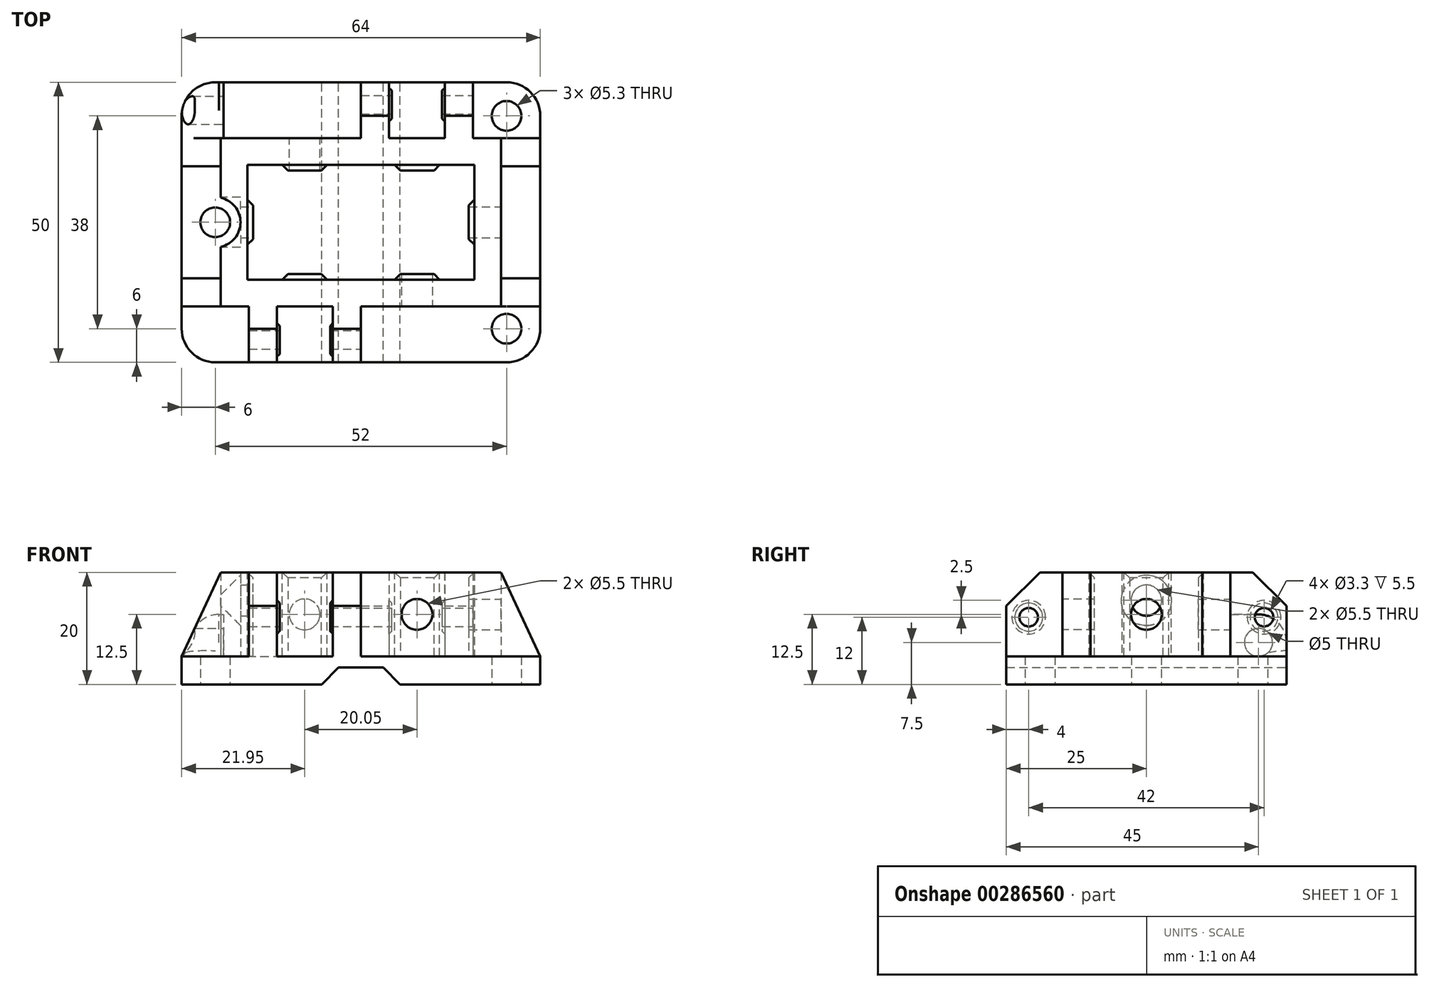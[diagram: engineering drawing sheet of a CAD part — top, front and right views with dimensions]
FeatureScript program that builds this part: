
annotation { "Feature Type Name" : "Feature", "Feature Type Description" : "" }
export const myFeature = defineFeature(function(context is Context, id is Id, definition is map)
    precondition{}
    {
        {
            var Q0;
            Q0=qCreatedBy(makeId("Top.planeOp"),FACE);
            var sketch = newSketch(context, id + "F0", { "sketchPlane" : qUnion([Q0])});
            skLineSegment(sketch, "E0.bottom", {"start": v(0, 0) * mm, "end": v(64, 0) * mm});
            skLineSegment(sketch, "E0.top", {"start": v(0, 50) * mm, "end": v(64, 50) * mm});
            skLineSegment(sketch, "E0.left", {"start": v(0, 0) * mm, "end": v(0, 50) * mm});
            skLineSegment(sketch, "E0.right", {"start": v(64, 0) * mm, "end": v(64, 50) * mm});
            skCircle(sketch, "E1", {"center": v(58, 44) * mm, "radius": 2.65 * mm});
            skPoint(sketch, "E2.centerSnap0", {"position": v(32, 0) * mm});
            skCircle(sketch, "E3", {"center": v(58, 6) * mm, "radius": 2.65 * mm});
            skCircle(sketch, "E4", {"center": v(6, 25) * mm, "radius": 2.65 * mm});
            skPoint(sketch, "E4.centerSnap0", {"position": v(0, 25) * mm});
            skSolve(sketch);
        }
        {
            var Q0;
            Q0=qSketchRegion(id+"F0",true);
            extrude(context, id + "F1", {"entities" : qUnion([Q0]), "depth" : 5 * mm});
        }
        {
            var Q0;
            Q0=makeQuery(id+"F1.opExtrude","CAP_FACE",FACE,{"disambiguationData":[OSD([sQuery(id+"F0.wireOp",EDGE,"E0.bottom"),sQuery(id+"F0.wireOp",EDGE,"E0.top"),sQuery(id+"F0.wireOp",EDGE,"E0.left"),sQuery(id+"F0.wireOp",EDGE,"E0.right"),sQuery(id+"F0.wireOp",EDGE,"SUFVuphh-Qgx9-THfo-SX6n-8QSMb4j17lpz"),sQuery(id+"F0.wireOp",EDGE,"E1"),sQuery(id+"F0.wireOp",EDGE,"E2")])],"isStart":false});
            var sketch = newSketch(context, id + "F2", { "sketchPlane" : qUnion([Q0])});
            skLineSegment(sketch, "E5.bottom", {"start": v(7, 40) * mm, "end": v(57, 40) * mm});
            skLineSegment(sketch, "E5.top", {"start": v(7, 10) * mm, "end": v(57, 10) * mm});
            skLineSegment(sketch, "E5.left", {"start": v(7, 40) * mm, "end": v(7, 29.39) * mm});
            skLineSegment(sketch, "E5.right", {"start": v(57, 40) * mm, "end": v(57, 10) * mm});
            skLineSegment(sketch, "E6.0.0", {"start": v(64, 50) * mm, "end": v(0, 50) * mm, "construction": true});
            skLineSegment(sketch, "E6.0.1", {"start": v(0, 50) * mm, "end": v(0, 0) * mm, "construction": true});
            skLineSegment(sketch, "E6.0.2", {"start": v(0, 0) * mm, "end": v(64, 0) * mm, "construction": true});
            skLineSegment(sketch, "E6.0.3", {"start": v(64, 0) * mm, "end": v(64, 50) * mm, "construction": true});
            skArc(sketch, "E7", {"start": v(7, 20.61) * mm, "mid": v(10.5, 25) * mm, "end": v(7, 29.39) * mm});
            skLineSegment(sketch, "E8.trimOffspring", {"start": v(7, 20.61) * mm, "end": v(7, 10) * mm});
            skLineSegment(sketch, "E9.bottom", {"start": v(11.75, 35.25) * mm, "end": v(52.25, 35.25) * mm});
            skLineSegment(sketch, "E9.top", {"start": v(11.75, 14.75) * mm, "end": v(52.25, 14.75) * mm});
            skLineSegment(sketch, "E9.left", {"start": v(11.75, 35.25) * mm, "end": v(11.75, 14.75) * mm});
            skLineSegment(sketch, "E9.right", {"start": v(52.25, 35.25) * mm, "end": v(52.25, 14.75) * mm});
            skSolve(sketch);
        }
        {
            var Q0;
            Q0=qSketchRegion(id+"F2",true);
            extrude(context, id + "F3", {"entities" : qUnion([Q0]), "operationType" : NewBodyOperationType.ADD, "depth" : 15 * mm});
        }
        {
            var Q0;
            Q0=makeQuery(id+"F3.opExtrude","CAP_FACE",FACE,{"disambiguationData":[OSD([sQuery(id+"F2.wireOp",EDGE,"E5.bottom"),sQuery(id+"F2.wireOp",EDGE,"E5.top"),sQuery(id+"F2.wireOp",EDGE,"E5.left"),sQuery(id+"F2.wireOp",EDGE,"E5.right"),sQuery(id+"F2.wireOp",EDGE,"E7"),sQuery(id+"F2.wireOp",EDGE,"E8.trimOffspring"),sQuery(id+"F2.wireOp",EDGE,"E9.bottom"),sQuery(id+"F2.wireOp",EDGE,"E9.top"),sQuery(id+"F2.wireOp",EDGE,"E9.left"),sQuery(id+"F2.wireOp",EDGE,"E9.right")])],"isStart":false});
            var sketch = newSketch(context, id + "F4", { "sketchPlane" : qUnion([Q0])});
            skLineSegment(sketch, "E10.bottom", {"start": v(11.75, 29) * mm, "end": v(12.75, 29) * mm});
            skLineSegment(sketch, "E10.top", {"start": v(11.75, 21) * mm, "end": v(12.75, 21) * mm});
            skLineSegment(sketch, "E10.left", {"start": v(11.75, 29) * mm, "end": v(11.75, 21) * mm});
            skLineSegment(sketch, "E10.right", {"start": v(12.75, 29) * mm, "end": v(12.75, 21) * mm});
            skLineSegment(sketch, "E11", {"start": v(32, 35.25) * mm, "end": v(32, 14.75) * mm, "construction": true});
            skLineSegment(sketch, "E12.MirrorCS", {"start": v(52.25, 29) * mm, "end": v(51.25, 29) * mm});
            skLineSegment(sketch, "E13.MirrorCS", {"start": v(52.25, 21) * mm, "end": v(51.25, 21) * mm});
            skLineSegment(sketch, "E14.MirrorCS", {"start": v(51.25, 29) * mm, "end": v(51.25, 21) * mm});
            skLineSegment(sketch, "E15.MirrorCS", {"start": v(52.25, 29) * mm, "end": v(52.25, 21) * mm});
            skLineSegment(sketch, "E16.bottom", {"start": v(38.05, 35.25) * mm, "end": v(46.05, 35.25) * mm});
            skLineSegment(sketch, "E16.top", {"start": v(38.05, 34.25) * mm, "end": v(46.05, 34.25) * mm});
            skLineSegment(sketch, "E16.left", {"start": v(38.05, 35.25) * mm, "end": v(38.05, 34.25) * mm});
            skLineSegment(sketch, "E16.right", {"start": v(46.05, 35.25) * mm, "end": v(46.05, 34.25) * mm});
            skLineSegment(sketch, "E17.bottom", {"start": v(17.95, 35.25) * mm, "end": v(25.95, 35.25) * mm});
            skLineSegment(sketch, "E17.top", {"start": v(17.95, 34.25) * mm, "end": v(25.95, 34.25) * mm});
            skLineSegment(sketch, "E17.left", {"start": v(17.95, 35.25) * mm, "end": v(17.95, 34.25) * mm});
            skLineSegment(sketch, "E17.right", {"start": v(25.95, 35.25) * mm, "end": v(25.95, 34.25) * mm});
            skLineSegment(sketch, "E18", {"start": v(52.25, 25) * mm, "end": v(11.75, 25) * mm, "construction": true});
            skLineSegment(sketch, "E19.MirrorCS", {"start": v(38.05, 14.75) * mm, "end": v(38.05, 15.75) * mm});
            skLineSegment(sketch, "E20.MirrorCS", {"start": v(17.95, 14.75) * mm, "end": v(17.95, 15.75) * mm});
            skLineSegment(sketch, "E21.MirrorCS", {"start": v(25.95, 14.75) * mm, "end": v(25.95, 15.75) * mm});
            skLineSegment(sketch, "E22.MirrorCS", {"start": v(46.05, 14.75) * mm, "end": v(46.05, 15.75) * mm});
            skLineSegment(sketch, "E23.MirrorCS", {"start": v(38.05, 14.75) * mm, "end": v(46.05, 14.75) * mm});
            skLineSegment(sketch, "E24.MirrorCS", {"start": v(17.95, 15.75) * mm, "end": v(25.95, 15.75) * mm});
            skLineSegment(sketch, "E25.MirrorCS", {"start": v(17.95, 14.75) * mm, "end": v(25.95, 14.75) * mm});
            skLineSegment(sketch, "E26.MirrorCS", {"start": v(38.05, 15.75) * mm, "end": v(46.05, 15.75) * mm});
            skSolve(sketch);
        }
        {
            var Q0;
            Q0=qSketchRegion(id+"F4",true);
            var Q1;
            Q1=makeQuery(id+"F3.boolean.opBoolean","SPLIT",FACE,{"disambiguationData":[TD([makeQuery(id+"F3.opExtrude","SWEPT_FACE",FACE,{"disambiguationData":[OSD([sQuery(id+"F2.wireOp",EDGE,"E9.bottom")])]})])],"derivedFrom":makeQuery(id+"F1.opExtrude","CAP_FACE",FACE,{"disambiguationData":[OSD([sQuery(id+"F0.wireOp",EDGE,"E0.bottom"),sQuery(id+"F0.wireOp",EDGE,"E0.top"),sQuery(id+"F0.wireOp",EDGE,"E0.left"),sQuery(id+"F0.wireOp",EDGE,"E0.right"),sQuery(id+"F0.wireOp",EDGE,"E1"),sQuery(id+"F0.wireOp",EDGE,"E3"),sQuery(id+"F0.wireOp",EDGE,"E4")])],"isStart":false})});
            extrude(context, id + "F5", {"entities" : qUnion([Q0]), "operationType" : NewBodyOperationType.ADD, "endBound" : BoundingType.UP_TO_SURFACE, "oppositeDirection" : true, "endBoundEntityFace" : qUnion([Q1]), "depth" : 25 * mm});
        }
        {
            var Q0;
            Q0=makeQuery(id+"F5.opExtrude","SWEPT_EDGE",EDGE,{"disambiguationData":[OSD([sQuery(id+"F4.wireOp",EDGE,"E10.bottom"),sQuery(id+"F4.wireOp",EDGE,"E10.right")])]});
            var Q1;
            Q1=makeQuery(id+"F5.opExtrude","SWEPT_EDGE",EDGE,{"disambiguationData":[OSD([sQuery(id+"F4.wireOp",EDGE,"E10.top"),sQuery(id+"F4.wireOp",EDGE,"E10.right")])]});
            var Q2;
            Q2=makeQuery(id+"F5.opExtrude","CAP_EDGE",EDGE,{"disambiguationData":[OSD([sQuery(id+"F4.wireOp",EDGE,"E10.right")])],"isStart":true});
            var Q3;
            Q3=makeQuery(id+"F5.opExtrude","SWEPT_EDGE",EDGE,{"disambiguationData":[OSD([sQuery(id+"F4.wireOp",EDGE,"E12.MirrorCS"),sQuery(id+"F4.wireOp",EDGE,"E14.MirrorCS")])]});
            var Q4;
            Q4=makeQuery(id+"F5.opExtrude","SWEPT_EDGE",EDGE,{"disambiguationData":[OSD([sQuery(id+"F4.wireOp",EDGE,"E13.MirrorCS"),sQuery(id+"F4.wireOp",EDGE,"E14.MirrorCS")])]});
            var Q5;
            Q5=makeQuery(id+"F5.opExtrude","CAP_EDGE",EDGE,{"disambiguationData":[OSD([sQuery(id+"F4.wireOp",EDGE,"E14.MirrorCS")])],"isStart":true});
            var Q6;
            Q6=makeQuery(id+"F5.opExtrude","SWEPT_EDGE",EDGE,{"disambiguationData":[OSD([sQuery(id+"F4.wireOp",EDGE,"E17.top"),sQuery(id+"F4.wireOp",EDGE,"E17.left")])]});
            var Q7;
            Q7=makeQuery(id+"F5.opExtrude","CAP_EDGE",EDGE,{"disambiguationData":[OSD([sQuery(id+"F4.wireOp",EDGE,"E17.top")])],"isStart":true});
            var Q8;
            Q8=makeQuery(id+"F5.opExtrude","SWEPT_EDGE",EDGE,{"disambiguationData":[OSD([sQuery(id+"F4.wireOp",EDGE,"E17.top"),sQuery(id+"F4.wireOp",EDGE,"E17.right")])]});
            var Q9;
            Q9=makeQuery(id+"F5.opExtrude","SWEPT_EDGE",EDGE,{"disambiguationData":[OSD([sQuery(id+"F4.wireOp",EDGE,"E16.top"),sQuery(id+"F4.wireOp",EDGE,"E16.left")])]});
            var Q10;
            Q10=makeQuery(id+"F5.opExtrude","CAP_EDGE",EDGE,{"disambiguationData":[OSD([sQuery(id+"F4.wireOp",EDGE,"E16.top")])],"isStart":true});
            var Q11;
            Q11=makeQuery(id+"F5.opExtrude","SWEPT_EDGE",EDGE,{"disambiguationData":[OSD([sQuery(id+"F4.wireOp",EDGE,"E16.top"),sQuery(id+"F4.wireOp",EDGE,"E16.right")])]});
            var Q12;
            Q12=makeQuery(id+"F5.opExtrude","CAP_EDGE",EDGE,{"disambiguationData":[OSD([sQuery(id+"F4.wireOp",EDGE,"E26.MirrorCS")])],"isStart":true});
            var Q13;
            Q13=makeQuery(id+"F5.opExtrude","CAP_EDGE",EDGE,{"disambiguationData":[OSD([sQuery(id+"F4.wireOp",EDGE,"E24.MirrorCS")])],"isStart":true});
            var Q14;
            Q14=makeQuery(id+"F5.opExtrude","SWEPT_EDGE",EDGE,{"disambiguationData":[OSD([sQuery(id+"F4.wireOp",EDGE,"E20.MirrorCS"),sQuery(id+"F4.wireOp",EDGE,"E24.MirrorCS")])]});
            var Q15;
            Q15=makeQuery(id+"F5.opExtrude","SWEPT_EDGE",EDGE,{"disambiguationData":[OSD([sQuery(id+"F4.wireOp",EDGE,"E21.MirrorCS"),sQuery(id+"F4.wireOp",EDGE,"E24.MirrorCS")])]});
            var Q16;
            Q16=makeQuery(id+"F5.opExtrude","SWEPT_EDGE",EDGE,{"disambiguationData":[OSD([sQuery(id+"F4.wireOp",EDGE,"E19.MirrorCS"),sQuery(id+"F4.wireOp",EDGE,"E26.MirrorCS")])]});
            var Q17;
            Q17=makeQuery(id+"F5.opExtrude","SWEPT_EDGE",EDGE,{"disambiguationData":[OSD([sQuery(id+"F4.wireOp",EDGE,"E22.MirrorCS"),sQuery(id+"F4.wireOp",EDGE,"E26.MirrorCS")])]});
            chamfer(context, id + "F6", {"entities" : qUnion([Q0, Q1, Q2, Q3, Q4, Q5, Q6, Q7, Q8, Q9, Q10, Q11, Q12, Q13, Q14, Q15, Q16, Q17]), "width" : 1 * mm, "tangentPropagation" : true});
        }
        {
            var Q0;
            Q0=makeQuery(id+"F1.opExtrude","SWEPT_EDGE",EDGE,{"disambiguationData":[OSD([sQuery(id+"F0.wireOp",EDGE,"E0.bottom"),sQuery(id+"F0.wireOp",EDGE,"E0.right")])]});
            var Q1;
            Q1=makeQuery(id+"F1.opExtrude","SWEPT_EDGE",EDGE,{"disambiguationData":[OSD([sQuery(id+"F0.wireOp",EDGE,"E0.top"),sQuery(id+"F0.wireOp",EDGE,"E0.left")])]});
            var Q2;
            Q2=makeQuery(id+"F1.opExtrude","SWEPT_EDGE",EDGE,{"disambiguationData":[OSD([sQuery(id+"F0.wireOp",EDGE,"E0.top"),sQuery(id+"F0.wireOp",EDGE,"E0.right")])]});
            var Q3;
            Q3=makeQuery(id+"F1.opExtrude","SWEPT_EDGE",EDGE,{"disambiguationData":[OSD([sQuery(id+"F0.wireOp",EDGE,"E0.bottom"),sQuery(id+"F0.wireOp",EDGE,"E0.left")])]});
            fillet(context, id + "F7", {"entities" : qUnion([Q0, Q1, Q2, Q3]), "radius" : 6 * mm, "tangentPropagation" : true, "allowEdgeOverflow" : false});
        }
        {
            var Q0;
            {var subQ0=sQuery(id+"F0.wireOp",EDGE,"E0.left");var subQ1=sQuery(id+"F0.wireOp",EDGE,"E4");var subQ2=sQuery(id+"F0.wireOp",EDGE,"E3");var subQ3=sQuery(id+"F0.wireOp",EDGE,"E1");var subQ4=sQuery(id+"F0.wireOp",EDGE,"E0.bottom");var subQ5=sQuery(id+"F0.wireOp",EDGE,"E0.right");var subQ6=sQuery(id+"F0.wireOp",EDGE,"E0.top");Q0=makeQuery(id+"F3.boolean.opBoolean","SPLIT",FACE,{"disambiguationData":[TD([makeQuery(id+"F1.opExtrude","SWEPT_FACE",FACE,{"disambiguationData":[OSD([subQ4])]})])],"derivedFrom":makeQuery(id+"F1.opExtrude","CAP_FACE",FACE,{"disambiguationData":[OSD([subQ4,subQ6,subQ0,subQ5,subQ3,subQ2,subQ1])],"isStart":false})});}
            var sketch = newSketch(context, id + "F8", { "sketchPlane" : qUnion([Q0])});
            skLineSegment(sketch, "E27.bottom", {"start": v(7, 40) * mm, "end": v(0, 40) * mm});
            skLineSegment(sketch, "E27.top", {"start": v(7, 35) * mm, "end": v(0, 35) * mm});
            skLineSegment(sketch, "E27.left", {"start": v(7, 40) * mm, "end": v(7, 35) * mm});
            skLineSegment(sketch, "E27.right", {"start": v(0, 40) * mm, "end": v(0, 35) * mm});
            skLineSegment(sketch, "E28.bottom", {"start": v(7, 10) * mm, "end": v(0, 10) * mm});
            skLineSegment(sketch, "E28.top", {"start": v(7, 15) * mm, "end": v(0, 15) * mm});
            skLineSegment(sketch, "E28.left", {"start": v(7, 10) * mm, "end": v(7, 15) * mm});
            skLineSegment(sketch, "E28.right", {"start": v(0, 10) * mm, "end": v(0, 15) * mm});
            skLineSegment(sketch, "E29.bottom", {"start": v(57, 40) * mm, "end": v(64, 40) * mm});
            skLineSegment(sketch, "E29.top", {"start": v(57, 35) * mm, "end": v(64, 35) * mm});
            skLineSegment(sketch, "E29.left", {"start": v(57, 40) * mm, "end": v(57, 35) * mm});
            skLineSegment(sketch, "E29.right", {"start": v(64, 40) * mm, "end": v(64, 35) * mm});
            skLineSegment(sketch, "E30.bottom", {"start": v(57, 10) * mm, "end": v(64, 10) * mm});
            skLineSegment(sketch, "E30.top", {"start": v(57, 15) * mm, "end": v(64, 15) * mm});
            skLineSegment(sketch, "E30.left", {"start": v(57, 10) * mm, "end": v(57, 15) * mm});
            skLineSegment(sketch, "E30.right", {"start": v(64, 10) * mm, "end": v(64, 15) * mm});
            skLineSegment(sketch, "E31.bottom", {"start": v(7, 10) * mm, "end": v(12.5, 10) * mm});
            skLineSegment(sketch, "E32.bottom", {"start": v(7, 40) * mm, "end": v(12.5, 40) * mm});
            skLineSegment(sketch, "E33.0.0", {"start": v(7, 20.61) * mm, "end": v(7, 10) * mm, "construction": true});
            skLineSegment(sketch, "E33.0.1", {"start": v(12.5, 10) * mm, "end": v(48.25, 10) * mm, "construction": true});
            skLineSegment(sketch, "E33.0.2", {"start": v(57, 10) * mm, "end": v(57, 40) * mm, "construction": true});
            skLineSegment(sketch, "E33.0.3", {"start": v(57, 40) * mm, "end": v(12.5, 40) * mm, "construction": true});
            skLineSegment(sketch, "E33.0.4", {"start": v(7, 40) * mm, "end": v(7, 29.39) * mm, "construction": true});
            skArc(sketch, "E33.0.5", {"start": v(7, 29.39) * mm, "mid": v(10.5, 25) * mm, "end": v(7, 20.61) * mm, "construction": true});
            skLineSegment(sketch, "E34.0", {"start": v(52.25, 35.25) * mm, "end": v(52.25, 29) * mm, "construction": true});
            skLineSegment(sketch, "E35.0", {"start": v(52.25, 21) * mm, "end": v(52.25, 14.75) * mm, "construction": true});
            skLineSegment(sketch, "E36.bottom", {"start": v(52, 40) * mm, "end": v(47, 40) * mm});
            skLineSegment(sketch, "E36.top", {"start": v(52, 50) * mm, "end": v(47, 50) * mm});
            skLineSegment(sketch, "E36.left", {"start": v(52, 40) * mm, "end": v(52, 50) * mm});
            skLineSegment(sketch, "E36.right", {"start": v(47, 40) * mm, "end": v(47, 50) * mm});
            skLineSegment(sketch, "E37.bottom", {"start": v(37, 50) * mm, "end": v(32, 50) * mm});
            skLineSegment(sketch, "E37.top", {"start": v(37, 40) * mm, "end": v(32, 40) * mm});
            skLineSegment(sketch, "E37.left", {"start": v(37, 50) * mm, "end": v(37, 40) * mm});
            skLineSegment(sketch, "E37.right", {"start": v(32, 50) * mm, "end": v(32, 40) * mm});
            skLineSegment(sketch, "E38.bottom", {"start": v(27, 10) * mm, "end": v(32, 10) * mm});
            skLineSegment(sketch, "E38.top", {"start": v(27, 0) * mm, "end": v(32, 0) * mm});
            skLineSegment(sketch, "E38.left", {"start": v(27, 10) * mm, "end": v(27, 0) * mm});
            skLineSegment(sketch, "E38.right", {"start": v(32, 10) * mm, "end": v(32, 0) * mm});
            skLineSegment(sketch, "E39.bottom", {"start": v(17, 10) * mm, "end": v(12, 10) * mm});
            skLineSegment(sketch, "E39.top", {"start": v(17, 0) * mm, "end": v(12, 0) * mm});
            skLineSegment(sketch, "E39.left", {"start": v(17, 10) * mm, "end": v(17, 0) * mm});
            skLineSegment(sketch, "E39.right", {"start": v(12, 10) * mm, "end": v(12, 0) * mm});
            skLineSegment(sketch, "E40.trimOffspring", {"start": v(52.25, 10) * mm, "end": v(57, 10) * mm, "construction": true});
            skSolve(sketch);
        }
        {
            var Q0;
            Q0=qSketchRegion(id+"F8",true);
            var Q1;
            Q1=makeQuery(id+"F5.boolean.opBoolean","MERGE",FACE,{"derivedFrom":[makeQuery(id+"F3.opExtrude","CAP_FACE",FACE,{"disambiguationData":[OSD([sQuery(id+"F2.wireOp",EDGE,"E5.bottom"),sQuery(id+"F2.wireOp",EDGE,"E5.top"),sQuery(id+"F2.wireOp",EDGE,"E5.left"),sQuery(id+"F2.wireOp",EDGE,"E5.right"),sQuery(id+"F2.wireOp",EDGE,"E7"),sQuery(id+"F2.wireOp",EDGE,"E8.trimOffspring"),sQuery(id+"F2.wireOp",EDGE,"E9.bottom"),sQuery(id+"F2.wireOp",EDGE,"E9.top"),sQuery(id+"F2.wireOp",EDGE,"E9.left"),sQuery(id+"F2.wireOp",EDGE,"E9.right")])],"isStart":false}),makeQuery(id+"F5.opExtrude","CAP_FACE",FACE,{"disambiguationData":[OSD([sQuery(id+"F4.wireOp",EDGE,"E10.bottom"),sQuery(id+"F4.wireOp",EDGE,"E10.top"),sQuery(id+"F4.wireOp",EDGE,"E10.left"),sQuery(id+"F4.wireOp",EDGE,"E10.right")])],"isStart":true}),makeQuery(id+"F5.opExtrude","CAP_FACE",FACE,{"disambiguationData":[OSD([sQuery(id+"F4.wireOp",EDGE,"E12.MirrorCS"),sQuery(id+"F4.wireOp",EDGE,"E13.MirrorCS"),sQuery(id+"F4.wireOp",EDGE,"E14.MirrorCS"),sQuery(id+"F4.wireOp",EDGE,"E15.MirrorCS")])],"isStart":true}),makeQuery(id+"F5.opExtrude","CAP_FACE",FACE,{"disambiguationData":[OSD([sQuery(id+"F4.wireOp",EDGE,"E16.bottom"),sQuery(id+"F4.wireOp",EDGE,"E16.top"),sQuery(id+"F4.wireOp",EDGE,"E16.left"),sQuery(id+"F4.wireOp",EDGE,"E16.right")])],"isStart":true}),makeQuery(id+"F5.opExtrude","CAP_FACE",FACE,{"disambiguationData":[OSD([sQuery(id+"F4.wireOp",EDGE,"E17.bottom"),sQuery(id+"F4.wireOp",EDGE,"E17.top"),sQuery(id+"F4.wireOp",EDGE,"E17.left"),sQuery(id+"F4.wireOp",EDGE,"E17.right")])],"isStart":true}),makeQuery(id+"F5.opExtrude","CAP_FACE",FACE,{"disambiguationData":[OSD([sQuery(id+"F4.wireOp",EDGE,"E19.MirrorCS"),sQuery(id+"F4.wireOp",EDGE,"E22.MirrorCS"),sQuery(id+"F4.wireOp",EDGE,"E23.MirrorCS"),sQuery(id+"F4.wireOp",EDGE,"E26.MirrorCS")])],"isStart":true}),makeQuery(id+"F5.opExtrude","CAP_FACE",FACE,{"disambiguationData":[OSD([sQuery(id+"F4.wireOp",EDGE,"E20.MirrorCS"),sQuery(id+"F4.wireOp",EDGE,"E21.MirrorCS"),sQuery(id+"F4.wireOp",EDGE,"E24.MirrorCS"),sQuery(id+"F4.wireOp",EDGE,"E25.MirrorCS")])],"isStart":true})]});
            extrude(context, id + "F9", {"entities" : qUnion([Q0]), "operationType" : NewBodyOperationType.ADD, "endBound" : BoundingType.UP_TO_SURFACE, "endBoundEntityFace" : qUnion([Q1]), "depth" : 25 * mm});
        }
        {
            var Q0;
            {var subQ0=makeQuery(id+"F9.opExtrude","SWEPT_FACE",FACE,{"disambiguationData":[OSD([sQuery(id+"F8.wireOp",EDGE,"E30.bottom")])]});var subQ1=makeQuery(id+"F9.opExtrude","SWEPT_FACE",FACE,{"disambiguationData":[OSD([sQuery(id+"F8.wireOp",EDGE,"E28.bottom")])]});var subQ2=makeQuery(id+"F3.opExtrude","SWEPT_FACE",FACE,{"disambiguationData":[OSD([sQuery(id+"F2.wireOp",EDGE,"E5.top")])]});Q0=qUnion([makeQuery(id+"F9.boolean.opBoolean","MERGE",FACE,{"disambiguationData":[OD(2.0)],"derivedFrom":[subQ2,subQ1,subQ0]}),makeQuery(id+"F9.boolean.opBoolean","MERGE",FACE,{"disambiguationData":[OD(0.0)],"derivedFrom":[subQ2,subQ1,subQ0]}),makeQuery(id+"F9.boolean.opBoolean","MERGE",FACE,{"disambiguationData":[OD(1.0)],"derivedFrom":[subQ2,subQ1,subQ0]})]);}
            var sketch = newSketch(context, id + "F10", { "sketchPlane" : qUnion([Q0])});
            skLineSegment(sketch, "E41", {"start": v(0, 5) * mm, "end": v(0, 20) * mm});
            skLineSegment(sketch, "E42.0.0", {"start": v(64, 20) * mm, "end": v(57, 20) * mm, "construction": true});
            skLineSegment(sketch, "E42.0.1", {"start": v(57, 20) * mm, "end": v(57, 5) * mm, "construction": true});
            skLineSegment(sketch, "E42.0.2", {"start": v(57, 5) * mm, "end": v(64, 5) * mm, "construction": true});
            skLineSegment(sketch, "E42.0.3", {"start": v(64, 5) * mm, "end": v(64, 20) * mm});
            skLineSegment(sketch, "E43", {"start": v(57, 20) * mm, "end": v(64, 20) * mm});
            skLineSegment(sketch, "E44", {"start": v(64, 5) * mm, "end": v(57, 20) * mm});
            skLineSegment(sketch, "E45.0.1", {"start": v(7, 20) * mm, "end": v(7, 5) * mm, "construction": true});
            skLineSegment(sketch, "E45.0.3", {"start": v(7, 5) * mm, "end": v(7, 20) * mm, "construction": true});
            skLineSegment(sketch, "E46", {"start": v(0, 20) * mm, "end": v(7, 20) * mm});
            skLineSegment(sketch, "E47", {"start": v(0, 5) * mm, "end": v(7, 20) * mm});
            skSolve(sketch);
        }
        {
            var Q0;
            Q0=qSketchRegion(id+"F10",true);
            var Q1;
            {var subQ0=makeQuery(id+"F9.opExtrude","SWEPT_FACE",FACE,{"disambiguationData":[OSD([sQuery(id+"F8.wireOp",EDGE,"E29.bottom")])]});var subQ1=makeQuery(id+"F9.opExtrude","SWEPT_FACE",FACE,{"disambiguationData":[OSD([sQuery(id+"F8.wireOp",EDGE,"E27.bottom")])]});var subQ2=makeQuery(id+"F3.opExtrude","SWEPT_FACE",FACE,{"disambiguationData":[OSD([sQuery(id+"F2.wireOp",EDGE,"E5.bottom")])]});Q1=qUnion([makeQuery(id+"F9.boolean.opBoolean","MERGE",FACE,{"disambiguationData":[OD(1.0)],"derivedFrom":[subQ2,subQ1,subQ0]}),makeQuery(id+"F9.boolean.opBoolean","MERGE",FACE,{"disambiguationData":[OD(2.0)],"derivedFrom":[subQ2,subQ1,subQ0]}),makeQuery(id+"F9.boolean.opBoolean","MERGE",FACE,{"disambiguationData":[OD(0.0)],"derivedFrom":[subQ2,subQ1,subQ0]})]);}
            extrude(context, id + "F11", {"entities" : qUnion([Q0]), "operationType" : NewBodyOperationType.REMOVE, "endBound" : BoundingType.UP_TO_SURFACE, "oppositeDirection" : true, "endBoundEntityFace" : qUnion([Q1]), "depth" : 25 * mm});
        }
        {
            var Q0;
            Q0=makeQuery(id+"F3.opExtrude","SWEPT_FACE",FACE,{"disambiguationData":[OSD([sQuery(id+"F2.wireOp",EDGE,"E5.right")])]});
            var sketch = newSketch(context, id + "F12", { "sketchPlane" : qUnion([Q0])});
            skCircle(sketch, "E48", {"center": v(25, 12.5) * mm, "radius": 2.75 * mm});
            skPoint(sketch, "E48.centerSnap0", {"position": v(35, 12.5) * mm});
            skPoint(sketch, "E48.centerSnap1", {"position": v(25, 20) * mm});
            skSolve(sketch);
        }
        {
            var Q0;
            Q0=qSketchRegion(id+"F12",true);
            var Q1;
            Q1=makeQuery(id+"F5.opExtrude","SWEPT_FACE",FACE,{"disambiguationData":[OSD([sQuery(id+"F4.wireOp",EDGE,"E14.MirrorCS")])]});
            extrude(context, id + "F13", {"entities" : qUnion([Q0]), "operationType" : NewBodyOperationType.REMOVE, "endBound" : BoundingType.UP_TO_SURFACE, "oppositeDirection" : true, "endBoundEntityFace" : qUnion([Q1]), "depth" : 25 * mm});
        }
        {
            var Q0;
            Q0=makeQuery(id+"F9.boolean.opBoolean","MERGE",FACE,{"disambiguationData":[OD(1.0)],"derivedFrom":[makeQuery(id+"F3.opExtrude","SWEPT_FACE",FACE,{"disambiguationData":[OSD([sQuery(id+"F2.wireOp",EDGE,"E5.bottom")])]}),makeQuery(id+"F9.opExtrude","SWEPT_FACE",FACE,{"disambiguationData":[OSD([sQuery(id+"F8.wireOp",EDGE,"E27.bottom")])]}),makeQuery(id+"F9.opExtrude","SWEPT_FACE",FACE,{"disambiguationData":[OSD([sQuery(id+"F8.wireOp",EDGE,"E29.bottom")])]})]});
            var sketch = newSketch(context, id + "F14", { "sketchPlane" : qUnion([Q0])});
            skCircle(sketch, "E49", {"center": v(-42.05, 12.5) * mm, "radius": 2.75 * mm, "construction": true});
            skPoint(sketch, "E49.centerSnap0", {"position": v(-47.05, 12.5) * mm});
            skCircle(sketch, "E50", {"center": v(-21.95, 12.5) * mm, "radius": 2.75 * mm});
            skLineSegment(sketch, "E51.0.0", {"start": v(-39.05, 5) * mm, "end": v(-45.05, 5) * mm, "construction": true});
            skLineSegment(sketch, "E51.0.1", {"start": v(-45.05, 5) * mm, "end": v(-45.05, 19) * mm, "construction": true});
            skLineSegment(sketch, "E51.0.2", {"start": v(-45.05, 19) * mm, "end": v(-39.05, 19) * mm, "construction": true});
            skLineSegment(sketch, "E51.0.3", {"start": v(-39.05, 19) * mm, "end": v(-39.05, 5) * mm, "construction": true});
            skSolve(sketch);
        }
        {
            var Q0;
            Q0=qSketchRegion(id+"F14",true);
            var Q1;
            Q1=makeQuery(id+"F5.opExtrude","SWEPT_FACE",FACE,{"disambiguationData":[OSD([sQuery(id+"F4.wireOp",EDGE,"E17.top")])]});
            extrude(context, id + "F15", {"entities" : qUnion([Q0]), "operationType" : NewBodyOperationType.REMOVE, "endBound" : BoundingType.UP_TO_SURFACE, "oppositeDirection" : true, "endBoundEntityFace" : qUnion([Q1]), "depth" : 25 * mm});
        }
        {
            var Q0;
            Q0=makeQuery(id+"F9.opExtrude","SWEPT_FACE",FACE,{"disambiguationData":[OSD([sQuery(id+"F8.wireOp",EDGE,"E36.left")])]});
            var sketch = newSketch(context, id + "F16", { "sketchPlane" : qUnion([Q0])});
            skCircle(sketch, "E52", {"center": v(46, 12) * mm, "radius": 1.65 * mm});
            skLineSegment(sketch, "E53.0.0", {"start": v(35, 20) * mm, "end": v(15, 20) * mm, "construction": true});
            skLineSegment(sketch, "E53.0.1", {"start": v(15, 20) * mm, "end": v(15, 5) * mm, "construction": true});
            skLineSegment(sketch, "E53.0.2", {"start": v(15, 5) * mm, "end": v(35, 5) * mm, "construction": true});
            skLineSegment(sketch, "E53.0.3", {"start": v(35, 5) * mm, "end": v(35, 20) * mm, "construction": true});
            skLineSegment(sketch, "E54", {"start": v(25, 20) * mm, "end": v(25, 5) * mm, "construction": true});
            skCircle(sketch, "E55.MirrorC", {"center": v(4, 12) * mm, "radius": 1.65 * mm});
            skSolve(sketch);
        }
        {
            var Q0;
            Q0=qSketchRegion(id+"F16",true);
            extrude(context, id + "F17", {"entities" : qUnion([Q0]), "operationType" : NewBodyOperationType.REMOVE, "endBound" : BoundingType.THROUGH_ALL, "oppositeDirection" : true, "depth" : 25 * mm});
        }
        {
            var Q0;
            Q0=makeQuery(id+"F9.opExtrude","CAP_EDGE",EDGE,{"disambiguationData":[OSD([sQuery(id+"F8.wireOp",EDGE,"E36.top")])],"isStart":false});
            var Q1;
            Q1=makeQuery(id+"F9.opExtrude","CAP_EDGE",EDGE,{"disambiguationData":[OSD([sQuery(id+"F8.wireOp",EDGE,"E37.bottom")])],"isStart":false});
            var Q2;
            Q2=makeQuery(id+"F9.opExtrude","CAP_EDGE",EDGE,{"disambiguationData":[OSD([sQuery(id+"F8.wireOp",EDGE,"E39.top")])],"isStart":false});
            var Q3;
            Q3=makeQuery(id+"F9.opExtrude","CAP_EDGE",EDGE,{"disambiguationData":[OSD([sQuery(id+"F8.wireOp",EDGE,"E38.top")])],"isStart":false});
            chamfer(context, id + "F18", {"entities" : qUnion([Q0, Q1, Q2, Q3]), "width" : 6 * mm, "tangentPropagation" : true});
        }
        {
            var Q0;
            Q0=makeQuery(id+"F3.opExtrude","SWEPT_FACE",FACE,{"disambiguationData":[OSD([sQuery(id+"F2.wireOp",EDGE,"E5.left")])]});
            var sketch = newSketch(context, id + "F19", { "sketchPlane" : qUnion([Q0])});
            skCircle(sketch, "E56", {"center": v(-25, 15) * mm, "radius": 4.5 * mm});
            skSolve(sketch);
        }
        {
            var Q0;
            Q0=qSketchRegion(id+"F19",true);
            extrude(context, id + "F20", {"entities" : qUnion([Q0]), "operationType" : NewBodyOperationType.REMOVE, "oppositeDirection" : true, "depth" : 3.5 * mm});
        }
        {
            var Q0;
            Q0=makeQuery(id+"F9.boolean.opBoolean","MERGE",FACE,{"disambiguationData":[OD(1.0)],"derivedFrom":[makeQuery(id+"F3.opExtrude","SWEPT_FACE",FACE,{"disambiguationData":[OSD([sQuery(id+"F2.wireOp",EDGE,"E5.top")])]}),makeQuery(id+"F9.opExtrude","SWEPT_FACE",FACE,{"disambiguationData":[OSD([sQuery(id+"F8.wireOp",EDGE,"E28.bottom")])]}),makeQuery(id+"F9.opExtrude","SWEPT_FACE",FACE,{"disambiguationData":[OSD([sQuery(id+"F8.wireOp",EDGE,"E30.bottom")])]})]});
            var sketch = newSketch(context, id + "F21", { "sketchPlane" : qUnion([Q0])});
            skLineSegment(sketch, "E57.0", {"start": v(46.05, 5) * mm, "end": v(46.05, 20) * mm, "construction": true});
            skLineSegment(sketch, "E58.0", {"start": v(38.05, 5) * mm, "end": v(38.05, 20) * mm, "construction": true});
            skLineSegment(sketch, "E59.0.0", {"start": v(11.75, 5) * mm, "end": v(17.95, 5) * mm, "construction": true});
            skLineSegment(sketch, "E59.0.1", {"start": v(17.95, 5) * mm, "end": v(18.95, 5) * mm, "construction": true});
            skLineSegment(sketch, "E59.0.2", {"start": v(18.95, 5) * mm, "end": v(24.95, 5) * mm, "construction": true});
            skLineSegment(sketch, "E59.0.3", {"start": v(24.95, 5) * mm, "end": v(25.95, 5) * mm, "construction": true});
            skLineSegment(sketch, "E59.0.4", {"start": v(25.95, 5) * mm, "end": v(38.05, 5) * mm, "construction": true});
            skLineSegment(sketch, "E59.0.5", {"start": v(38.05, 5) * mm, "end": v(39.05, 5) * mm, "construction": true});
            skLineSegment(sketch, "E59.0.6", {"start": v(39.05, 5) * mm, "end": v(45.05, 5) * mm, "construction": true});
            skLineSegment(sketch, "E59.0.7", {"start": v(45.05, 5) * mm, "end": v(46.05, 5) * mm, "construction": true});
            skLineSegment(sketch, "E59.0.8", {"start": v(46.05, 5) * mm, "end": v(52.25, 5) * mm, "construction": true});
            skLineSegment(sketch, "E59.0.10", {"start": v(52.25, 5) * mm, "end": v(51.25, 5) * mm, "construction": true});
            skLineSegment(sketch, "E59.0.12", {"start": v(51.25, 5) * mm, "end": v(52.25, 5) * mm, "construction": true});
            skLineSegment(sketch, "E59.0.14", {"start": v(52.25, 5) * mm, "end": v(46.05, 5) * mm, "construction": true});
            skLineSegment(sketch, "E59.0.15", {"start": v(46.05, 5) * mm, "end": v(45.05, 5) * mm, "construction": true});
            skLineSegment(sketch, "E59.0.16", {"start": v(45.05, 5) * mm, "end": v(39.05, 5) * mm, "construction": true});
            skLineSegment(sketch, "E59.0.17", {"start": v(39.05, 5) * mm, "end": v(38.05, 5) * mm, "construction": true});
            skLineSegment(sketch, "E59.0.18", {"start": v(38.05, 5) * mm, "end": v(25.95, 5) * mm, "construction": true});
            skLineSegment(sketch, "E59.0.19", {"start": v(25.95, 5) * mm, "end": v(24.95, 5) * mm, "construction": true});
            skLineSegment(sketch, "E59.0.20", {"start": v(24.95, 5) * mm, "end": v(18.95, 5) * mm, "construction": true});
            skLineSegment(sketch, "E59.0.21", {"start": v(18.95, 5) * mm, "end": v(17.95, 5) * mm, "construction": true});
            skLineSegment(sketch, "E59.0.22", {"start": v(17.95, 5) * mm, "end": v(11.75, 5) * mm, "construction": true});
            skLineSegment(sketch, "E59.0.24", {"start": v(11.75, 5) * mm, "end": v(12.75, 5) * mm, "construction": true});
            skLineSegment(sketch, "E59.0.26", {"start": v(12.75, 5) * mm, "end": v(11.75, 5) * mm, "construction": true});
            skLineSegment(sketch, "E60.0.1", {"start": v(27, 20) * mm, "end": v(32, 20) * mm, "construction": true});
            skLineSegment(sketch, "E60.0.3", {"start": v(32, 20) * mm, "end": v(57, 20) * mm, "construction": true});
            skLineSegment(sketch, "E60.0.7", {"start": v(57, 20) * mm, "end": v(52, 20) * mm, "construction": true});
            skLineSegment(sketch, "E60.0.9", {"start": v(52, 20) * mm, "end": v(47, 20) * mm, "construction": true});
            skLineSegment(sketch, "E60.0.11", {"start": v(47, 20) * mm, "end": v(37, 20) * mm, "construction": true});
            skLineSegment(sketch, "E60.0.13", {"start": v(37, 20) * mm, "end": v(32, 20) * mm, "construction": true});
            skLineSegment(sketch, "E60.0.15", {"start": v(32, 20) * mm, "end": v(7, 20) * mm, "construction": true});
            skLineSegment(sketch, "E60.0.18", {"start": v(7, 20) * mm, "end": v(10.5, 20) * mm, "construction": true});
            skLineSegment(sketch, "E60.0.21", {"start": v(7, 20) * mm, "end": v(12, 20) * mm, "construction": true});
            skLineSegment(sketch, "E60.0.23", {"start": v(12, 20) * mm, "end": v(17, 20) * mm, "construction": true});
            skLineSegment(sketch, "E60.0.25", {"start": v(17, 20) * mm, "end": v(27, 20) * mm, "construction": true});
            skCircle(sketch, "E61", {"center": v(42, 12.5) * mm, "radius": 2.75 * mm});
            skPoint(sketch, "E61.centerSnap0", {"position": v(42, 20) * mm});
            skPoint(sketch, "E61.centerSnap1", {"position": v(38.05, 12.5) * mm});
            skSolve(sketch);
        }
        {
            var Q0;
            Q0=qSketchRegion(id+"F21",true);
            var Q1;
            Q1=makeQuery(id+"F5.opExtrude","SWEPT_FACE",FACE,{"disambiguationData":[OSD([sQuery(id+"F4.wireOp",EDGE,"E26.MirrorCS")])]});
            extrude(context, id + "F22", {"entities" : qUnion([Q0]), "operationType" : NewBodyOperationType.REMOVE, "endBound" : BoundingType.UP_TO_SURFACE, "oppositeDirection" : true, "endBoundEntityFace" : qUnion([Q1]), "depth" : 25 * mm});
        }
        {
            var Q0;
            Q0=makeQuery(id+"F9.opExtrude","SWEPT_FACE",FACE,{"disambiguationData":[OSD([sQuery(id+"F8.wireOp",EDGE,"E36.right")])]});
            var sketch = newSketch(context, id + "F23", { "sketchPlane" : qUnion([Q0])});
            skCircle(sketch, "E62.0", {"center": v(-46, 12) * mm, "radius": 1.65 * mm});
            skCircle(sketch, "E63", {"center": v(-46, 12) * mm, "radius": 3 * mm});
            skSolve(sketch);
        }
        {
            var Q0;
            Q0=qSketchRegion(id+"F23",true);
            extrude(context, id + "F24", {"entities" : qUnion([Q0]), "operationType" : NewBodyOperationType.ADD, "depth" : .5 * mm});
        }
        {
            var Q0;
            Q0=makeQuery(id+"F9.opExtrude","SWEPT_FACE",FACE,{"disambiguationData":[OSD([sQuery(id+"F8.wireOp",EDGE,"E37.left")])]});
            var sketch = newSketch(context, id + "F25", { "sketchPlane" : qUnion([Q0])});
            skCircle(sketch, "E64.0", {"center": v(46, 12) * mm, "radius": 1.65 * mm});
            skCircle(sketch, "E65", {"center": v(46, 12) * mm, "radius": 3 * mm});
            skSolve(sketch);
        }
        {
            var Q0;
            Q0=qSketchRegion(id+"F25",true);
            extrude(context, id + "F26", {"entities" : qUnion([Q0]), "operationType" : NewBodyOperationType.ADD, "depth" : .5 * mm});
        }
        {
            var Q0;
            Q0=makeQuery(id+"F9.opExtrude","SWEPT_FACE",FACE,{"disambiguationData":[OSD([sQuery(id+"F8.wireOp",EDGE,"E38.left")])]});
            var sketch = newSketch(context, id + "F27", { "sketchPlane" : qUnion([Q0])});
            skCircle(sketch, "E66", {"center": v(-4, 12) * mm, "radius": 3 * mm});
            skCircle(sketch, "E67.0", {"center": v(-4, 12) * mm, "radius": 1.65 * mm});
            skSolve(sketch);
        }
        {
            var Q0;
            Q0=qSketchRegion(id+"F27",true);
            extrude(context, id + "F28", {"entities" : qUnion([Q0]), "operationType" : NewBodyOperationType.ADD, "depth" : .5 * mm});
        }
        {
            var Q0;
            Q0=makeQuery(id+"F9.opExtrude","SWEPT_FACE",FACE,{"disambiguationData":[OSD([sQuery(id+"F8.wireOp",EDGE,"E39.left")])]});
            var sketch = newSketch(context, id + "F29", { "sketchPlane" : qUnion([Q0])});
            skCircle(sketch, "E68.0", {"center": v(4, 12) * mm, "radius": 1.65 * mm});
            skCircle(sketch, "E69", {"center": v(4, 12) * mm, "radius": 3 * mm});
            skSolve(sketch);
        }
        {
            var Q0;
            Q0=qSketchRegion(id+"F29",true);
            extrude(context, id + "F30", {"entities" : qUnion([Q0]), "operationType" : NewBodyOperationType.ADD, "depth" : .5 * mm});
        }
        {
            var Q0;
            Q0=makeQuery(id+"F30.opExtrude","CAP_EDGE",EDGE,{"disambiguationData":[OSD([sQuery(id+"F29.wireOp",EDGE,"E69")])],"isStart":false});
            var Q1;
            Q1=makeQuery(id+"F28.opExtrude","CAP_EDGE",EDGE,{"disambiguationData":[OSD([sQuery(id+"F27.wireOp",EDGE,"E66")])],"isStart":false});
            var Q2;
            Q2=makeQuery(id+"F26.opExtrude","CAP_EDGE",EDGE,{"disambiguationData":[OSD([sQuery(id+"F25.wireOp",EDGE,"E65")])],"isStart":false});
            var Q3;
            Q3=makeQuery(id+"F24.opExtrude","CAP_EDGE",EDGE,{"disambiguationData":[OSD([sQuery(id+"F23.wireOp",EDGE,"E63")])],"isStart":false});
            chamfer(context, id + "F31", {"entities" : qUnion([Q0, Q1, Q2, Q3]), "width" : .5 * mm, "tangentPropagation" : true});
        }
        {
            var Q0;
            Q0=makeQuery(id+"F9.boolean.opBoolean","MERGE",FACE,{"derivedFrom":[makeQuery(id+"F1.opExtrude","SWEPT_FACE",FACE,{"disambiguationData":[OSD([sQuery(id+"F0.wireOp",EDGE,"E0.top")])]}),makeQuery(id+"F9.opExtrude","SWEPT_FACE",FACE,{"disambiguationData":[OSD([sQuery(id+"F8.wireOp",EDGE,"E36.top")])]}),makeQuery(id+"F9.opExtrude","SWEPT_FACE",FACE,{"disambiguationData":[OSD([sQuery(id+"F8.wireOp",EDGE,"E37.bottom")])]})]});
            var sketch = newSketch(context, id + "F32", { "sketchPlane" : qUnion([Q0])});
            skLineSegment(sketch, "E70", {"start": v(-39, 0) * mm, "end": v(-36, 3) * mm});
            skLineSegment(sketch, "E71", {"start": v(-36, 3) * mm, "end": v(-28, 3) * mm});
            skLineSegment(sketch, "E72", {"start": v(-28, 3) * mm, "end": v(-25, 0) * mm});
            skLineSegment(sketch, "E73", {"start": v(-39, 0) * mm, "end": v(-25, 0) * mm});
            skSolve(sketch);
        }
        {
            var Q0;
            Q0=qSketchRegion(id+"F32",true);
            extrude(context, id + "F33", {"entities" : qUnion([Q0]), "operationType" : NewBodyOperationType.REMOVE, "endBound" : BoundingType.THROUGH_ALL, "oppositeDirection" : true, "depth" : 25 * mm});
        }
        {
            var Q0;
            Q0=makeQuery(id+"F9.boolean.opBoolean","MERGE",FACE,{"derivedFrom":[makeQuery(id+"F1.opExtrude","SWEPT_FACE",FACE,{"disambiguationData":[OSD([sQuery(id+"F0.wireOp",EDGE,"E0.left")])]}),makeQuery(id+"F9.opExtrude","SWEPT_FACE",FACE,{"disambiguationData":[OSD([sQuery(id+"F8.wireOp",EDGE,"E27.right")])]}),makeQuery(id+"F9.opExtrude","SWEPT_FACE",FACE,{"disambiguationData":[OSD([sQuery(id+"F8.wireOp",EDGE,"E28.right")])]})]});
            cPlane(context, id + "F34", {"entities" : qUnion([Q0]), "cplaneType" : CPlaneType.OFFSET, "offset" : 7.5 * mm, "oppositeDirection" : true, "width" : 150 * mm, "height" : 150 * mm});
        }
        {
            var Q0;
            Q0=qCreatedBy(id+"F34.planeOp",FACE);
            var sketch = newSketch(context, id + "F35", { "sketchPlane" : qUnion([Q0])});
            skLineSegment(sketch, "E74.0.0", {"start": v(-35, 5) * mm, "end": v(-40, 5) * mm, "construction": true});
            skLineSegment(sketch, "E74.0.1", {"start": v(-40, 5) * mm, "end": v(-44, 5) * mm, "construction": true});
            skLineSegment(sketch, "E74.0.2", {"start": v(-44, 5) * mm, "end": v(-44, 0) * mm, "construction": true});
            skLineSegment(sketch, "E74.0.3", {"start": v(-44, 0) * mm, "end": v(-6, 0) * mm, "construction": true});
            skLineSegment(sketch, "E74.0.4", {"start": v(-6, 0) * mm, "end": v(-6, 5) * mm, "construction": true});
            skLineSegment(sketch, "E74.0.5", {"start": v(-6, 5) * mm, "end": v(-10, 5) * mm, "construction": true});
            skLineSegment(sketch, "E74.0.6", {"start": v(-10, 5) * mm, "end": v(-15, 5) * mm, "construction": true});
            skLineSegment(sketch, "E74.0.7", {"start": v(-15, 5) * mm, "end": v(-35, 5) * mm, "construction": true});
            skLineSegment(sketch, "E75.0.0", {"start": v(-44, 5) * mm, "end": v(-50, 5) * mm, "construction": true});
            skLineSegment(sketch, "E75.0.1", {"start": v(-50, 0) * mm, "end": v(-50, 5) * mm, "construction": true});
            skLineSegment(sketch, "E75.0.2", {"start": v(-44, 0) * mm, "end": v(-50, 0) * mm, "construction": true});
            skLineSegment(sketch, "E75.0.3", {"start": v(-44, 0) * mm, "end": v(-44, 5) * mm, "construction": true});
            skLineSegment(sketch, "E76.0.0", {"start": v(-40, 20) * mm, "end": v(-44, 20) * mm, "construction": true});
            skLineSegment(sketch, "E76.0.1", {"start": v(-44, 20) * mm, "end": v(-50, 14) * mm, "construction": true});
            skLineSegment(sketch, "E76.0.2", {"start": v(-50, 14) * mm, "end": v(-50, 5) * mm, "construction": true});
            skLineSegment(sketch, "E76.0.3", {"start": v(-50, 5) * mm, "end": v(-40, 5) * mm, "construction": true});
            skLineSegment(sketch, "E76.0.4", {"start": v(-40, 5) * mm, "end": v(-40, 20) * mm, "construction": true});
            skArc(sketch, "E77", {"start": v(-45, 12.5) * mm, "mid": v(-48.54, 11.04) * mm, "end": v(-50, 7.5) * mm});
            skLineSegment(sketch, "E78", {"start": v(-50, 7.5) * mm, "end": v(-50, 5) * mm});
            skLineSegment(sketch, "E79", {"start": v(-40, 5) * mm, "end": v(-50, 5) * mm});
            skLineSegment(sketch, "E80", {"start": v(-40, 7.5) * mm, "end": v(-40, 5) * mm});
            skLineSegment(sketch, "E81", {"start": v(-45, 12.5) * mm, "end": v(-40, 12.5) * mm});
            skLineSegment(sketch, "E82", {"start": v(-40, 12.5) * mm, "end": v(-40, 7.5) * mm});
            skSolve(sketch);
        }
        {
            var Q0;
            Q0 = qSketchRegion(id + "F35", true);
            var Q1;
            Q1=makeQuery(id+"F9.boolean.opBoolean","MERGE",FACE,{"derivedFrom":[makeQuery(id+"F1.opExtrude","SWEPT_FACE",FACE,{"disambiguationData":[OSD([sQuery(id+"F0.wireOp",EDGE,"E0.left")])]}),makeQuery(id+"F9.opExtrude","SWEPT_FACE",FACE,{"disambiguationData":[OSD([sQuery(id+"F8.wireOp",EDGE,"E27.right")])]}),makeQuery(id+"F9.opExtrude","SWEPT_FACE",FACE,{"disambiguationData":[OSD([sQuery(id+"F8.wireOp",EDGE,"E28.right")])]})]});
            extrude(context, id + "F36", {"entities" : qUnion([Q0]), "operationType" : NewBodyOperationType.ADD, "endBound" : BoundingType.UP_TO_SURFACE, "endBoundEntityFace" : qUnion([Q1]), "depth" : 25 * mm});
        }
        {
            var Q0;
            Q0=makeQuery(id+"F36.opExtrude","SWEPT_FACE",FACE,{"disambiguationData":[OSD([sQuery(id+"F35.wireOp",EDGE,"E79")])]});
            var sketch = newSketch(context, id + "F37", { "sketchPlane" : qUnion([Q0])});
            skLineSegment(sketch, "E83.0.0", {"start": v(0, -50) * mm, "end": v(6, -50) * mm});
            skArc(sketch, "E83.0.1", {"start": v(6, -50) * mm, "mid": v(1.76, -48.24) * mm, "end": v(0, -44) * mm});
            skLineSegment(sketch, "E83.0.2", {"start": v(0, -44) * mm, "end": v(0, -50) * mm});
            skSolve(sketch);
        }
        {
            var Q0;
            Q0 = qSketchRegion(id + "F37", true);
            extrude(context, id + "F38", {"entities" : qUnion([Q0]), "operationType" : NewBodyOperationType.REMOVE, "endBound" : BoundingType.THROUGH_ALL, "oppositeDirection" : true, "depth" : 25 * mm});
        }
        {
            var Q0;
            Q0=makeQuery(id+"F36.boolean.opBoolean","MERGE",FACE,{"derivedFrom":[makeQuery(id+"F9.boolean.opBoolean","MERGE",FACE,{"derivedFrom":[makeQuery(id+"F1.opExtrude","SWEPT_FACE",FACE,{"disambiguationData":[OSD([sQuery(id+"F0.wireOp",EDGE,"E0.top")])]}),makeQuery(id+"F9.opExtrude","SWEPT_FACE",FACE,{"disambiguationData":[OSD([sQuery(id+"F8.wireOp",EDGE,"E36.top")])]}),makeQuery(id+"F9.opExtrude","SWEPT_FACE",FACE,{"disambiguationData":[OSD([sQuery(id+"F8.wireOp",EDGE,"E37.bottom")])]})]}),makeQuery(id+"F36.opExtrude","SWEPT_FACE",FACE,{"disambiguationData":[OSD([sQuery(id+"F35.wireOp",EDGE,"E78")])]})]});
            var sketch = newSketch(context, id + "F39", { "sketchPlane" : qUnion([Q0])});
            skLineSegment(sketch, "E84.0.0", {"start": v(0, 5) * mm, "end": v(-7, 20) * mm, "construction": true});
            skLineSegment(sketch, "E84.0.2", {"start": v(-7, 20) * mm, "end": v(-3.5, 12.5) * mm, "construction": true});
            skLineSegment(sketch, "E84.0.3", {"start": v(-3.5, 12.5) * mm, "end": v(0, 5) * mm, "construction": true});
            skLineSegment(sketch, "E85.0.0", {"start": v(0, 12.5) * mm, "end": v(-0.08, 12.5) * mm, "construction": true});
            skLineSegment(sketch, "E85.0.2", {"start": v(0, 12.5) * mm, "end": v(-3.5, 12.5) * mm, "construction": true});
            skLineSegment(sketch, "E85.0.3", {"start": v(-3.5, 12.5) * mm, "end": v(-7.5, 12.5) * mm, "construction": true});
            skLineSegment(sketch, "E85.0.5", {"start": v(-7.5, 12.5) * mm, "end": v(-0.08, 12.5) * mm, "construction": true});
            skLineSegment(sketch, "E86.0.1", {"start": v(0, 12.5) * mm, "end": v(0, 0) * mm, "construction": true});
            skLineSegment(sketch, "E86.0.3", {"start": v(0, 0) * mm, "end": v(0, 5) * mm, "construction": true});
            skLineSegment(sketch, "E86.0.8", {"start": v(0, 5) * mm, "end": v(0, 12.5) * mm, "construction": true});
            skLineSegment(sketch, "E87", {"start": v(-3.5, 12.5) * mm, "end": v(0, 12.5) * mm});
            skLineSegment(sketch, "E88", {"start": v(0, 12.5) * mm, "end": v(0, 5) * mm});
            skLineSegment(sketch, "E89", {"start": v(0, 5) * mm, "end": v(-3.5, 12.5) * mm});
            skSolve(sketch);
        }
        {
            var Q0;
            Q0 = qSketchRegion(id + "F39", true);
            extrude(context, id + "F40", {"entities" : qUnion([Q0]), "operationType" : NewBodyOperationType.REMOVE, "endBound" : BoundingType.THROUGH_ALL, "oppositeDirection" : true, "depth" : 25 * mm});
        }
        {
            var Q0;
            Q0=makeQuery(id+"F36.opExtrude","CAP_FACE",FACE,{"disambiguationData":[OSD([sQuery(id+"F35.wireOp",EDGE,"E77"),sQuery(id+"F35.wireOp",EDGE,"E78"),sQuery(id+"F35.wireOp",EDGE,"E79"),sQuery(id+"F35.wireOp",EDGE,"E80"),sQuery(id+"F35.wireOp",EDGE,"E81"),sQuery(id+"F35.wireOp",EDGE,"E82")])],"isStart":true});
            var sketch = newSketch(context, id + "F41", { "sketchPlane" : qUnion([Q0])});
            skArc(sketch, "E90.0.0", {"start": v(48.94, 10.57) * mm, "mid": v(47.2, 12) * mm, "end": v(45, 12.5) * mm, "construction": true});
            skArc(sketch, "E90.0.2", {"start": v(45, 12.5) * mm, "mid": v(48.54, 11.04) * mm, "end": v(50, 7.5) * mm, "construction": true});
            skArc(sketch, "E90.0.4", {"start": v(50, 7.5) * mm, "mid": v(49.73, 9.12) * mm, "end": v(48.94, 10.57) * mm, "construction": true});
            skCircle(sketch, "E91", {"center": v(45, 7.5) * mm, "radius": 2.5 * mm});
            skSolve(sketch);
        }
        {
            var Q0;
            Q0 = qSketchRegion(id + "F41", true);
            extrude(context, id + "F42", {"entities" : qUnion([Q0]), "operationType" : NewBodyOperationType.REMOVE, "endBound" : BoundingType.THROUGH_ALL, "oppositeDirection" : true, "depth" : 25 * mm});
        }
        {
            var Q0;
            Q0=makeQuery(id+"F40.boolean.opBoolean","INTERSECT",EDGE,{"derivedFrom":[makeQuery(id+"F36.opExtrude","SWEPT_FACE",FACE,{"disambiguationData":[OSD([sQuery(id+"F35.wireOp",EDGE,"E77")])]}),makeQuery(id+"F40.opExtrude","SWEPT_FACE",FACE,{"disambiguationData":[OSD([sQuery(id+"F39.wireOp",EDGE,"E89")])]})]});
            fillet(context, id + "F43", {"entities" : qUnion([Q0]), "radius" : 5 * mm, "tangentPropagation" : true, "allowEdgeOverflow" : false});
        }
        {
            var Q0;
            Q0=makeQuery(id+"F5.opExtrude","SWEPT_FACE",FACE,{"disambiguationData":[OSD([sQuery(id+"F4.wireOp",EDGE,"E10.right")])]});
            var sketch = newSketch(context, id + "F44", { "sketchPlane" : qUnion([Q0])});
            skArc(sketch, "E92.0", {"start": v(20.61, 16) * mm, "mid": v(22.2, 18.52) * mm, "end": v(25, 19.5) * mm, "construction": true});
            skCircle(sketch, "E93", {"center": v(25, 15) * mm, "radius": 2.75 * mm});
            skSolve(sketch);
        }
        {
            var Q0;
            Q0 = qSketchRegion(id + "F44", true);
            var Q1;
            Q1=makeQuery(id+"F3.opExtrude","SWEPT_FACE",FACE,{"disambiguationData":[OSD([sQuery(id+"F2.wireOp",EDGE,"E5.left")])]});
            extrude(context, id + "F45", {"entities" : qUnion([Q0]), "operationType" : NewBodyOperationType.REMOVE, "endBound" : BoundingType.UP_TO_SURFACE, "oppositeDirection" : true, "endBoundEntityFace" : qUnion([Q1]), "depth" : 25 * mm});
        }
    });
